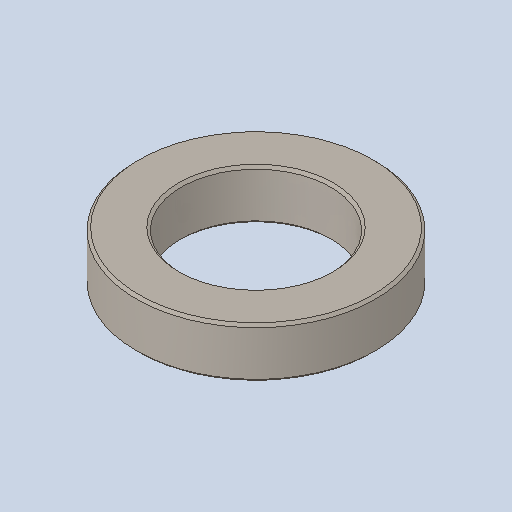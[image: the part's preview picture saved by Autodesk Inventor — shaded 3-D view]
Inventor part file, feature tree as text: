
AUTODESK INVENTOR PART (.ipt)
format: ipt  version: 2023.4 (Build 274418000, 418)  size: 101,888 bytes
history: native  units: in
note: dims shown in document units (in); Inventor stores cm internally (conversion verified against a paired STEP export)
features: chamfer x1
ambient origin geometry x8: Origin, YZ Plane, XZ Plane, XY Plane, X Axis, Y Axis, Z Axis, Center Point
bodies: Solid1 (feature_tree)
feature tree (1):
  chamfer  "Chamfer1"  [1 undecoded]
note: 1 required parameter value undecoded (feature->parameter linkage not recoverable at this tier; creation-order binding heuristic only, values carry confidence <= 0.55)
